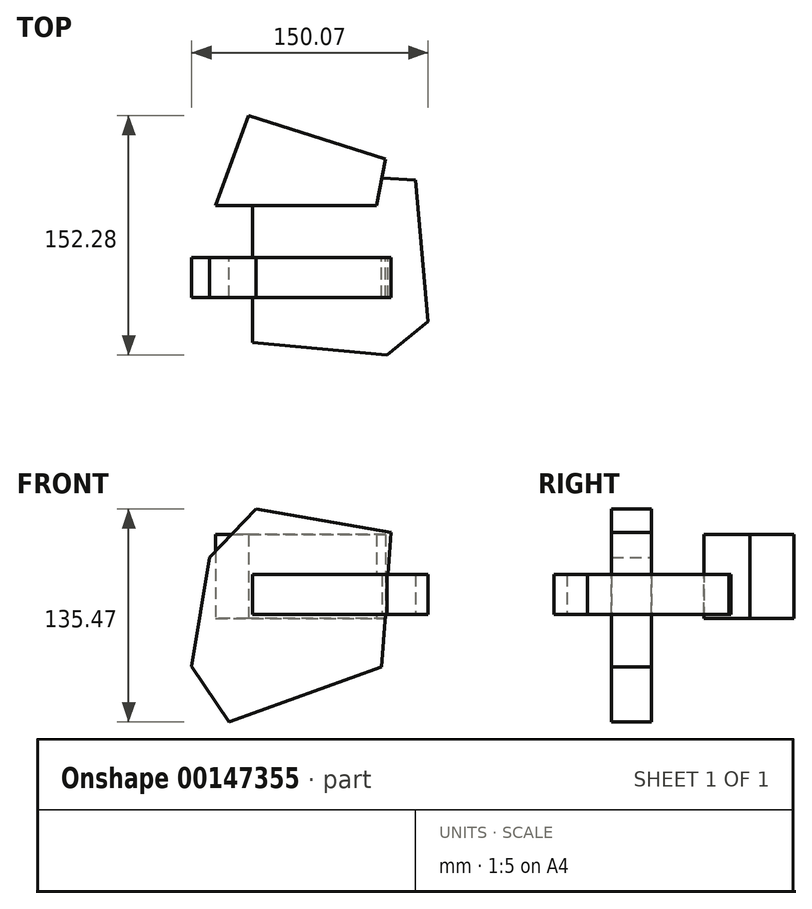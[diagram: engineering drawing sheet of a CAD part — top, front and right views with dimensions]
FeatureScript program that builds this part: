
annotation { "Feature Type Name" : "Feature", "Feature Type Description" : "" }
export const myFeature = defineFeature(function(context is Context, id is Id, definition is map)
    precondition{}
    {
        {
            var Q0;
            Q0=qCreatedBy(makeId("Front.planeOp"),FACE);
            var sketch = newSketch(context, id + "F0", { "sketchPlane" : qUnion([Q0])});
            skLineSegment(sketch, "E0", {"start": v(-42.4, 67.17) * mm, "end": v(-72, 36.19) * mm});
            skLineSegment(sketch, "E1", {"start": v(-72, 36.19) * mm, "end": v(-83.22, -33) * mm});
            skLineSegment(sketch, "E2", {"start": v(-83.22, -33) * mm, "end": v(-59.44, -68.3) * mm});
            skLineSegment(sketch, "E3", {"start": v(-59.44, -68.3) * mm, "end": v(37.46, -33.15) * mm});
            skLineSegment(sketch, "E4", {"start": v(37.46, -33.15) * mm, "end": v(43.3, 51.98) * mm});
            skLineSegment(sketch, "E5", {"start": v(43.3, 51.98) * mm, "end": v(-42.4, 67.17) * mm});
            skSolve(sketch);
        }
        {
            var Q0;
            Q0 = qSketchRegion(id + "F0", true);
            extrude(context, id + "F1", {"entities" : qUnion([Q0]), "depth" : 25.4 * mm});
        }
        {
            var Q0;
            Q0=qCreatedBy(makeId("Top.planeOp"),FACE);
            var sketch = newSketch(context, id + "F2", { "sketchPlane" : qUnion([Q0])});
            skLineSegment(sketch, "E6", {"start": v(-44.47, 55.6) * mm, "end": v(-44.47, -53.85) * mm});
            skLineSegment(sketch, "E7", {"start": v(-44.47, -53.85) * mm, "end": v(40.8, -62.03) * mm});
            skLineSegment(sketch, "E8", {"start": v(40.8, -62.03) * mm, "end": v(66.85, -40.67) * mm});
            skLineSegment(sketch, "E9", {"start": v(66.85, -40.67) * mm, "end": v(58.82, 49.18) * mm});
            skLineSegment(sketch, "E10", {"start": v(58.82, 49.18) * mm, "end": v(-44.47, 55.6) * mm});
            skSolve(sketch);
        }
        {
            var Q0;
            Q0=makeQuery(id+"F2.imprint","IMPRINT",FACE,{"disambiguationData":[TD([[makeQuery(id+"F2.imprint","IMPRINT",EDGE,{"derivedFrom":sQuery(id+"F2.wireOp",EDGE,"E6")}),1.0]])]});
            extrude(context, id + "F3", {"entities" : qUnion([Q0]), "operationType" : NewBodyOperationType.ADD, "depth" : 25.4 * mm});
        }
        {
            var Q0;
            Q0=makeQuery(id+"F3.opExtrude","CAP_FACE",FACE,{"disambiguationData":[OSD([sQuery(id+"F2.wireOp",EDGE,"E6"),sQuery(id+"F2.wireOp",EDGE,"E7"),sQuery(id+"F2.wireOp",EDGE,"E8"),sQuery(id+"F2.wireOp",EDGE,"E9"),sQuery(id+"F2.wireOp",EDGE,"E10")])],"isStart":false});
            var sketch = newSketch(context, id + "F4", { "sketchPlane" : qUnion([Q0])});
            skLineSegment(sketch, "E11", {"start": v(34.04, 33.1) * mm, "end": v(39.9, 62.43) * mm});
            skLineSegment(sketch, "E12", {"start": v(39.9, 62.43) * mm, "end": v(-47.3, 90.25) * mm});
            skLineSegment(sketch, "E13", {"start": v(-47.3, 90.25) * mm, "end": v(-68.06, 33.1) * mm});
            skLineSegment(sketch, "E14", {"start": v(-68.06, 33.1) * mm, "end": v(34.04, 33.1) * mm});
            skSolve(sketch);
        }
        {
            var Q0;
            {var subQ6=sQuery(id+"F4.wireOp",EDGE,"E12");Q0=makeQuery(id+"F4.imprint","IMPRINT",FACE,{"disambiguationData":[TD([[makeQuery(id+"F4.imprint","IMPRINT",EDGE,{"derivedFrom":subQ6}),1.0]])]});}
            var Q1;
            {var subQ0=sQuery(id+"F4.wireOp",EDGE,"E14");var subQ1=sQuery(id+"F4.wireOp",EDGE,"E11");var subQ2=makeQuery(id+"F4.imprint","INTERSECT",VERTEX,{"derivedFrom":[subQ1,subQ0]});Q1=makeQuery(id+"F4.imprint","IMPRINT",FACE,{"disambiguationData":[TD([[makeQuery(id+"F4.imprint","IMPRINT",EDGE,{"disambiguationData":[TD([[subQ2,-1.0]])],"derivedFrom":subQ1}),1.0]])]});}
            extrude(context, id + "F5", {"entities" : qUnion([Q0, Q1]), "operationType" : NewBodyOperationType.ADD, "depth" : 25.4 * mm, "hasSecondDirection" : true, "secondDirectionOppositeDirection" : true, "secondDirectionDepth" : 27.94 * mm});
        }
    });
